# Revit family: Crest Boiler-Hellcat FCB1000-6000
name_source: partatom
category: Mechanical Equipment
revit_build: Autodesk Revit 2017 (Build: 20190507_1515(x64)
units: mm (PartAtom-declared; Revit-internal decimal feet)

## family parameters
Always vertical = Yes
Cut with Voids When Loaded = No
OmniClass Number = 23.65.35.11.17
OmniClass Title = Thermodynamic Water Heaters
Part Type = Normal
Room Calculation Point = No
Round Connector Dimension = Use Radius
Shared = No
Work Plane-Based = No

## types (8) — shared parameters
# of Electrical Connections = 1
Back Clearance = 24"
Description = CREST Condensing Boiler with Hellcat Combustion Technology
FUEL TYPE = NATURAL GAS
Front Clearance = 30"
Fuel Type = Natural
Left Clearance = 24"
Manufacturer = Lochinvar
Right Clearance = 24"
SES BIM Studio # = 21 0649 01
Top Clearance = 24"
URL = http://www.lochinvar.com
Voltage/Control = 24

## per-type parameters (varying)
- FCB1000: AIR INLET SIZE=6"; A_HEIGHT=78"; Air Inlet Radius=3"; B_WIDTH=30"; Back of Unit to CL of Vent=1"; C_Depth to Condensate End=56"; Curve Position=6"; D_Water Outlet Offset=57 1/2"; E_Water Outlet Height=66 1/8"; F_Water Inlet Height=11 7/8"; GALLON CAPACITY=77; GAS CONN SIZE=1 1/4"; G_Boiler Drain Height=11 3/8"; Gas Conn Radius=5/8"; INPUT RATE (BTUH)=999,000; K_DEPTH=55 1/2"; L_Depth to Vent=51 3/4"; M_Air Inlet Offset=12 3/4"; N_Air Inlet Offset=6 1/2"; O_Width to Gas=26"; P_Gas Conn Offset=21 1/2"; R_ Vent Offset=6 1/2"; Total Amps (FLA)=6.0; VENT SIZE=6"; Vent Radius=3"; Voltage/Heater=120V/1PH/60Hz; WATER CONN SIZE=3"; Water Conn Radius=1 1/2"
- FCB1500: AIR INLET SIZE=8"; A_HEIGHT=78"; Air Inlet Radius=4"; B_WIDTH=30"; Back of Unit to CL of Vent=1"; C_Depth to Condensate End=63 3/4"; Curve Position=6"; D_Water Outlet Offset=64"; E_Water Outlet Height=65 3/8"; F_Water Inlet Height=12 3/8"; GALLON CAPACITY=94; GAS CONN SIZE=1 1/2"; G_Boiler Drain Height=11 3/8"; Gas Conn Radius=3/4"; INPUT RATE (BTUH)=1,500,000; K_DEPTH=63 1/4"; L_Depth to Vent=58 1/4"; M_Air Inlet Offset=13 1/4"; N_Air Inlet Offset=7 1/2"; O_Width to Gas=25 3/4"; P_Gas Conn Offset=23 1/4"; R_ Vent Offset=5 1/8"; Total Amps (FLA)=10.0; VENT SIZE=8"; Vent Radius=4"; Voltage/Heater=120V/1PH/60Hz; WATER CONN SIZE=4"; Water Conn Radius=2"
- FCB2000: AIR INLET SIZE=8"; A_HEIGHT=78"; Air Inlet Radius=4"; B_WIDTH=30"; Back of Unit to CL of Vent=1"; C_Depth to Condensate End=62 1/2"; Curve Position=6"; D_Water Outlet Offset=64 1/4"; E_Water Outlet Height=65 3/8"; F_Water Inlet Height=12 3/8"; GALLON CAPACITY=111; GAS CONN SIZE=1 1/2"; G_Boiler Drain Height=11 3/8"; Gas Conn Radius=3/4"; INPUT RATE (BTUH)=1,999,000; K_DEPTH=62 1/4"; L_Depth to Vent=57 1/4"; M_Air Inlet Offset=12"; N_Air Inlet Offset=7 1/2"; O_Width to Gas=26"; P_Gas Conn Offset=21 1/2"; R_ Vent Offset=5 1/8"; Total Amps (FLA)=13.0; VENT SIZE=8"; Vent Radius=4"; Voltage/Heater=120V/1PH/60Hz; WATER CONN SIZE=4"; Water Conn Radius=2"
- FCB2500: AIR INLET SIZE=8"; A_HEIGHT=77 3/4"; Air Inlet Radius=4"; B_WIDTH=35"; Back of Unit to CL of Vent=1"; C_Depth to Condensate End=79 1/4"; Curve Position=7 1/4"; D_Water Outlet Offset=79 1/4"; E_Water Outlet Height=63 3/4"; F_Water Inlet Height=13 1/2"; GALLON CAPACITY=157; GAS CONN SIZE=2"; G_Boiler Drain Height=11 1/4"; Gas Conn Radius=1"; INPUT RATE (BTUH)=2,500,000; K_DEPTH=79"; L_Depth to Vent=71 3/4"; M_Air Inlet Offset=17 1/4"; N_Air Inlet Offset=9 1/4"; O_Width to Gas=30 1/4"; P_Gas Conn Offset=28"; R_ Vent Offset=7 1/4"; Total Amps (FLA)=4.5; VENT SIZE=9"; Vent Radius=4 1/2"; Voltage/Heater=208V/3PH/60Hz; WATER CONN SIZE=4"; Water Conn Radius=2"
- FCB3000: AIR INLET SIZE=10"; A_HEIGHT=77 3/4"; Air Inlet Radius=5"; B_WIDTH=35"; Back of Unit to CL of Vent=2"; C_Depth to Condensate End=79 1/4"; Curve Position=7 1/4"; D_Water Outlet Offset=79 1/4"; E_Water Outlet Height=63 3/4"; F_Water Inlet Height=13 1/2"; GALLON CAPACITY=156; GAS CONN SIZE=2"; G_Boiler Drain Height=11 1/4"; Gas Conn Radius=1"; INPUT RATE (BTUH)=3,000,000; K_DEPTH=79"; L_Depth to Vent=71 3/4"; M_Air Inlet Offset=17 1/4"; N_Air Inlet Offset=9 1/4"; O_Width to Gas=30 1/4"; P_Gas Conn Offset=28"; R_ Vent Offset=7 1/4"; Total Amps (FLA)=6.5; VENT SIZE=10"; Vent Radius=5"; Voltage/Heater=208V/3PH/60Hz; WATER CONN SIZE=4"; Water Conn Radius=2"
- FCB4000: AIR INLET SIZE=12"; A_HEIGHT=78"; Air Inlet Radius=6"; B_WIDTH=43 1/4"; Back of Unit to CL of Vent=3"; C_Depth to Condensate End=95 1/4"; Curve Position=9 5/16"; D_Water Outlet Offset=90 3/4"; E_Water Outlet Height=63 1/2"; F_Water Inlet Height=13 3/4"; GALLON CAPACITY=201; GAS CONN SIZE=2 1/2"; G_Boiler Drain Height=11 1/2"; Gas Conn Radius=1 1/4"; INPUT RATE (BTUH)=3,999,000; K_DEPTH=94 3/4"; L_Depth to Vent=85 3/4"; M_Air Inlet Offset=19"; N_Air Inlet Offset=11 1/4"; O_Width to Gas=36 1/2"; P_Gas Conn Offset=35"; R_ Vent Offset=10 1/2"; Total Amps (FLA)=6.0; VENT SIZE=12"; Vent Radius=6"; Voltage/Heater=480V/3PH/60Hz; WATER CONN SIZE=4"; Water Conn Radius=2"
- FCB5000: AIR INLET SIZE=14"; A_HEIGHT=78"; Air Inlet Radius=7"; B_WIDTH=46 1/2"; Back of Unit to CL of Vent=3"; C_Depth to Condensate End=96 1/2"; Curve Position=10 1/8"; D_Water Outlet Offset=94"; E_Water Outlet Height=63 1/2"; F_Water Inlet Height=15"; GALLON CAPACITY=254; GAS CONN SIZE=2 1/2"; G_Boiler Drain Height=11 1/2"; Gas Conn Radius=1 1/4"; INPUT RATE (BTUH)=4,999,000; K_DEPTH=96 1/4"; L_Depth to Vent=87"; M_Air Inlet Offset=18 3/4"; N_Air Inlet Offset=13"; O_Width to Gas=39 3/4"; P_Gas Conn Offset=34"; R_ Vent Offset=9"; Total Amps (FLA)=5.0; VENT SIZE=14"; Vent Radius=7"; Voltage/Heater=480V/3PH/60Hz; WATER CONN SIZE=6"; Water Conn Radius=3"
- FCB6000: AIR INLET SIZE=14"; A_HEIGHT=78"; Air Inlet Radius=7"; B_WIDTH=50"; Back of Unit to CL of Vent=1"; C_Depth to Condensate End=102 3/4"; Curve Position=11"; D_Water Outlet Offset=99 3/4"; E_Water Outlet Height=63 1/4"; F_Water Inlet Height=14 3/4"; GALLON CAPACITY=304; GAS CONN SIZE=3"; G_Boiler Drain Height=11 1/2"; Gas Conn Radius=1 1/2"; INPUT RATE (BTUH)=6,000,000; K_DEPTH=96 1/2"; L_Depth to Vent=87 1/2"; M_Air Inlet Offset=16 1/2"; N_Air Inlet Offset=14 3/4"; O_Width to Gas=43 1/4"; P_Gas Conn Offset=29 3/4"; R_ Vent Offset=9 1/4"; Total Amps (FLA)=7.0; VENT SIZE=14"; Vent Radius=7"; Voltage/Heater=480V/3PH/60Hz; WATER CONN SIZE=6"; Water Conn Radius=3"

note: column(s) folded — value = type name in every type: MODEL NO., Model

## geometry (parser evidence)
native form markers: Sweep x2
no freeform markers — native parametric forms only
